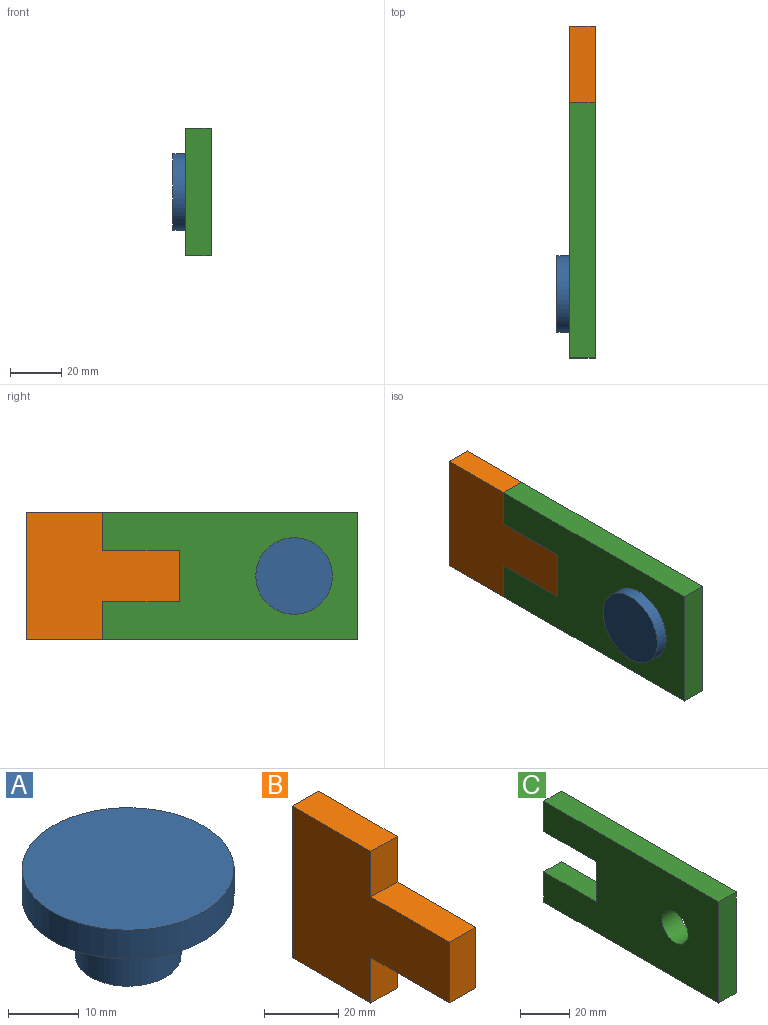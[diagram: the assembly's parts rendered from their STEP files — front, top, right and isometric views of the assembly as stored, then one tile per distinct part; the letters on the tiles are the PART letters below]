
ASSEMBLY  parts=3 mates=5
PART A: 5 faces, bbox 30x30x15 mm
  f0: cylinder r=7.5mm len=15mm, axis (0,0,-1), area 471.2mm2, adj f1,f4
  f1: plane 15x15mm, normal (0,0,-1), area 176.7mm2, adj f0
  f2: cylinder r=15mm len=30mm, axis (0,0,-1), area 471.2mm2, adj f3,f4
  f3: plane 30x30mm, normal (0,0,1), area 706.9mm2, adj f2
  f4: plane 30x30mm, normal (0,0,-1), area 530.1mm2, adj f0,f2
PART B: 10 faces, bbox 10x60x50 mm
  f0: plane 20x10mm, normal (0,-1,0), area 200mm2, adj f1,f2,f6,f8
  f1: plane 60x50mm, normal (1,0,0), area 2100mm2, adj f0,f3,f4,f5,f6,f7,f8,f9
  f2: plane 60x50mm, normal (-1,0,0), area 2100mm2, adj f0,f3,f4,f5,f6,f7,f8,f9
  f3: plane 30x10mm, normal (0,0,-1), area 300mm2, adj f1,f2,f4,f7
  f4: plane 50x10mm, normal (0,1,0), area 500mm2, adj f1,f2,f3,f5
  f5: plane 30x10mm, normal (0,0,1), area 300mm2, adj f1,f2,f4,f9
  f6: plane 30x10mm, normal (0,0,-1), area 300mm2, adj f0,f1,f2,f7
  f7: plane 15x10mm, normal (0,-1,0), area 150mm2, adj f1,f2,f3,f6
  f8: plane 30x10mm, normal (0,0,1), area 300mm2, adj f0,f1,f2,f9
  f9: plane 15x10mm, normal (0,-1,0), area 150mm2, adj f1,f2,f5,f8
PART C: 11 faces, bbox 10x100x50 mm
  f0: plane 15x10mm, normal (0,1,0), area 150mm2, adj f1,f2,f5,f8
  f1: plane 100x50mm, normal (1,0,0), area 4223.3mm2, adj f0,f3,f4,f5,f6,f7,f8,f9
  f2: plane 100x50mm, normal (-1,0,0), area 4223.3mm2, adj f0,f3,f4,f5,f6,f7,f8,f9
  f3: plane 100x10mm, normal (0,0,-1), area 1000mm2, adj f1,f2,f4,f6
  f4: plane 15x10mm, normal (0,1,0), area 150mm2, adj f1,f2,f3,f7
  f5: plane 100x10mm, normal (0,0,1), area 1000mm2, adj f0,f1,f2,f6
  f6: plane 50x10mm, normal (0,-1,0), area 500mm2, adj f1,f2,f3,f5
  f7: plane 30x10mm, normal (0,0,1), area 300mm2, adj f1,f2,f4,f9
  f8: plane 30x10mm, normal (0,0,-1), area 300mm2, adj f0,f1,f2,f9
  f9: plane 20x10mm, normal (0,1,0), area 200mm2, adj f1,f2,f7,f8
  f10: cylinder r=7.5mm len=15mm, axis (1,0,0), area 471.2mm2, adj f1,f2
PLACE A rot(axis=(-0.58,-0.58,0.58),120deg) t=(-7.06,-26.05,8.88)mm
PLACE B t=(-17.06,78.95,-16.12)mm
PLACE C t=(-17.06,48.95,-16.12)mm fixed
MATE planar B.f5 <-> C.f5  axis (0,0,1) through (-12.06,63.95,33.88)mm
MATE planar B.f1 <-> C.f1  axis (1,0,0) through (-7.06,55.38,8.88)mm
MATE planar A.f2 <-> C.f2  axis (1,0,0) through (-17.06,-26.05,8.88)mm
MATE planar B.f0 <-> C.f9  axis (0,-1,0) through (-12.06,18.95,8.88)mm
MATE cylindrical C.f10 <-> A.f0  axis (1,0,0) through (-7.06,-26.05,8.88)mm
